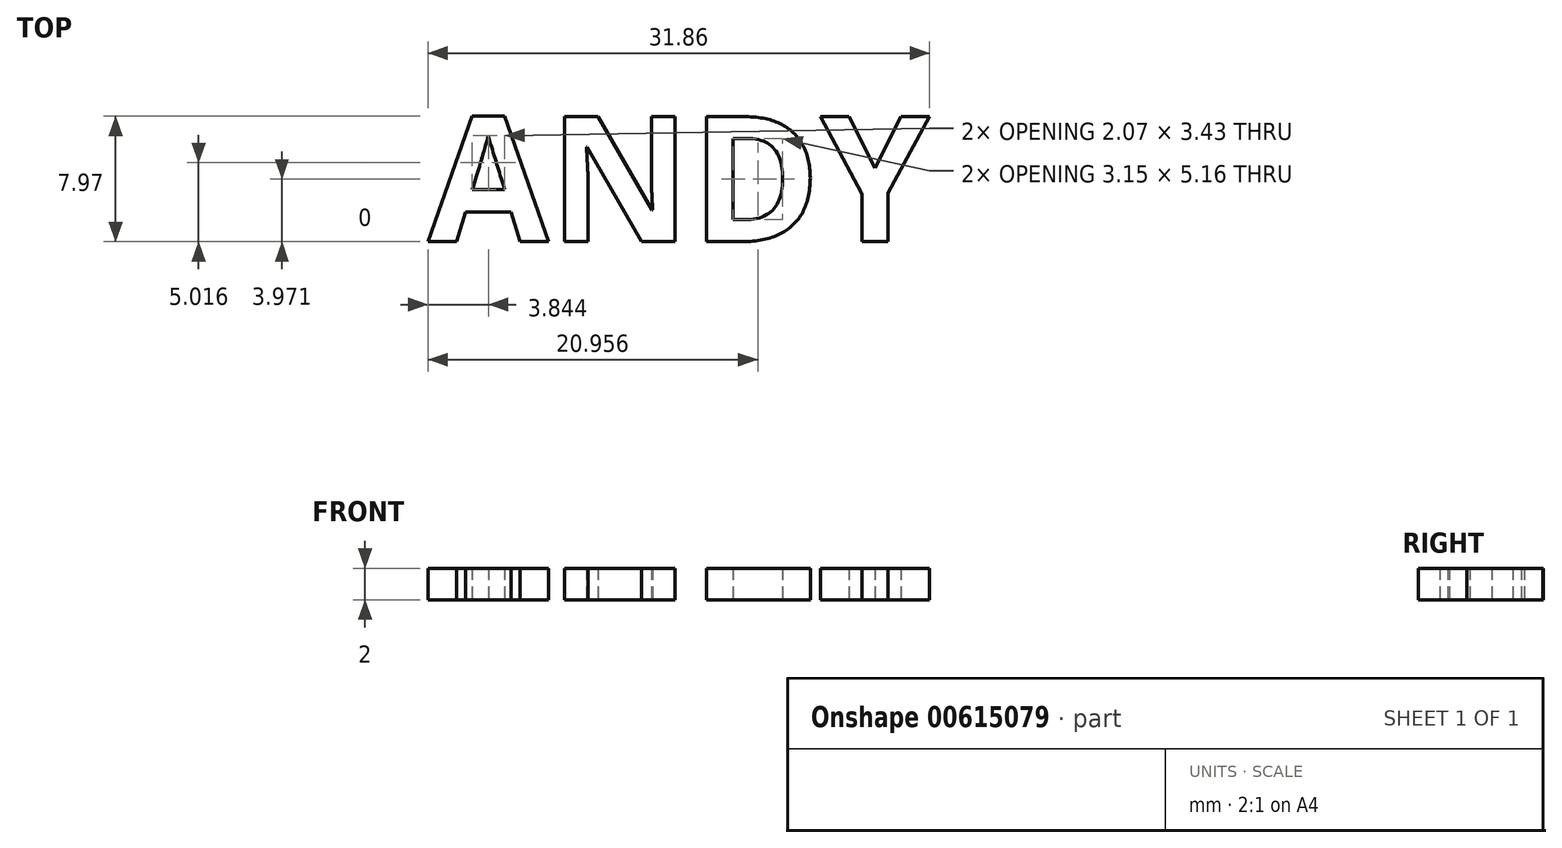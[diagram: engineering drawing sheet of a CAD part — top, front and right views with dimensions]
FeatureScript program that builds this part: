
annotation { "Feature Type Name" : "Feature", "Feature Type Description" : "" }
export const myFeature = defineFeature(function(context is Context, id is Id, definition is map)
    precondition{}
    {
        {
            var Q0;
            Q0=qCreatedBy(makeId("Top.planeOp"),FACE);
            var sketch = newSketch(context, id + "F0", { "sketchPlane" : qUnion([Q0])});
            skText(sketch, "E0", { "text": "ANDY", "fontName": "OpenSans-Bold.ttf"});
            const initialGuessF0  = {"E0": [0.00744, 0.00879, 1, 0, 0.008]};
            skSetInitialGuess(sketch, initialGuessF0);
            skSolve(sketch);
        }
        {
            var Q0;
            Q0=makeQuery(id+"F0.imprint","IMPRINT",FACE,{"disambiguationData":[TD([[makeQuery(id+"F0.imprint","IMPRINT",EDGE,{"derivedFrom":sQuery(id+"F0.wireOp",EDGE,"E0.sketch_text.stroke-0")}),-1.0]])]});
            var Q1;
            Q1=makeQuery(id+"F0.imprint","IMPRINT",FACE,{"disambiguationData":[TD([[makeQuery(id+"F0.imprint","IMPRINT",EDGE,{"derivedFrom":sQuery(id+"F0.wireOp",EDGE,"E0.sketch_text.stroke-12")}),-1.0]])]});
            var Q2;
            Q2=makeQuery(id+"F0.imprint","IMPRINT",FACE,{"disambiguationData":[TD([[makeQuery(id+"F0.imprint","IMPRINT",EDGE,{"derivedFrom":sQuery(id+"F0.wireOp",EDGE,"E0.sketch_text.stroke-26")}),-1.0]])]});
            var Q3;
            Q3=makeQuery(id+"F0.imprint","IMPRINT",FACE,{"disambiguationData":[TD([[makeQuery(id+"F0.imprint","IMPRINT",EDGE,{"derivedFrom":sQuery(id+"F0.wireOp",EDGE,"E0.sketch_text.stroke-38")}),-1.0]])]});
            extrude(context, id + "F1", {"entities" : qUnion([Q0, Q1, Q2, Q3]), "depth" : 2 * mm, "offsetDistance" : 25 * mm});
        }
    });
